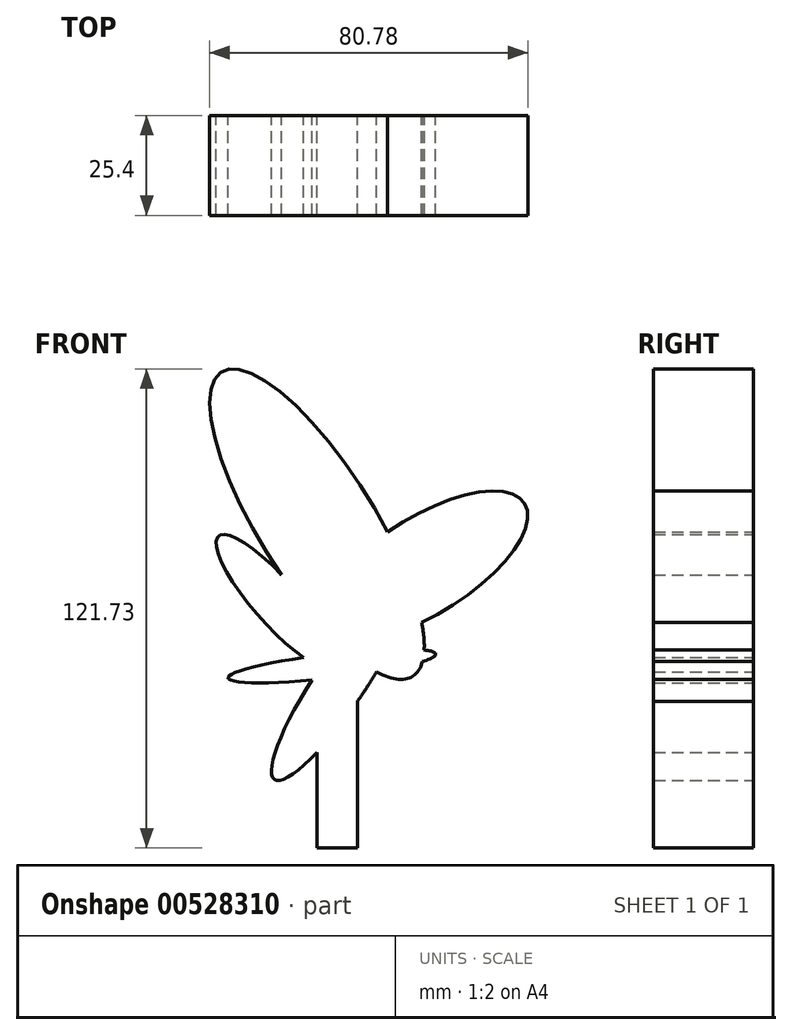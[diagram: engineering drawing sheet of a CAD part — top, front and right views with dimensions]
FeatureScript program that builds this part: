
annotation { "Feature Type Name" : "Feature", "Feature Type Description" : "" }
export const myFeature = defineFeature(function(context is Context, id is Id, definition is map)
    precondition{}
    {
        {
            var Q0;
            Q0=qCreatedBy(makeId("Front.planeOp"),FACE);
            var sketch = newSketch(context, id + "F0", { "sketchPlane" : qUnion([Q0])});
            skLineSegment(sketch, "E0", {"start": v(-21.42, 2.55) * mm, "end": v(-21.42, -21.8) * mm});
            skLineSegment(sketch, "E1", {"start": v(-11.19, 15.4) * mm, "end": v(-11.19, -21.8) * mm});
            skEllipticalArc(sketch, "E2", {});
            skEllipticalArc(sketch, "E3", {});
            skEllipticalArc(sketch, "E4", {});
            skEllipticalArc(sketch, "E5.trimOffspring", {});
            skEllipticalArc(sketch, "E6.trimOffspring", {});
            skEllipticalArc(sketch, "E7.trimOffspring", {});
            skEllipticalArc(sketch, "E8.trimOffspring", {});
            skEllipticalArc(sketch, "E9.trimOffspring", {});
            skEllipticalArc(sketch, "E10.trimOffspring", {});
            skPoint(sketch, "E11.orphan", {"position": v(-21.42, 19.53) * mm});
            skLineSegment(sketch, "E12", {"start": v(-21.42, -21.8) * mm, "end": v(-11.19, -21.8) * mm});
            skEllipticalArc(sketch, "E13.trimOffspring", {});
            const initialGuessF0  = {"E2": [-0.03204191848635339, 0.040952984243628865, 0.6578915012340197, -0.75311272237564, 0.021902368200880307, 0.0056739378525159905, 1.754059745511126, 5.502237001774265], "E3": [0.006067109759896994, 0.05005364865064621, -0.8483565072771697, -0.5294253833737872, 0.029723851108698438, 0.012318866726651034, 1.283638110579809, 4.833864496009394], "E4": [-0.021424479782577985, 0.06048149242996919, 0.5314910901465612, -0.8470638825347354, 0.045661041475952874, 0.014620046839002173, 5.771778276653766, 0.28550303601651894], "E5.trimOffspring": [-0.01763253659009599, 0.024458032101390248, 0.9934402020267449, 0.11435280930987413, 0.02652802497607398, 0.0030641987160904614, 1.8335367287470163, 4.506809050935362], "E6.trimOffspring": [-0.015736564993858337, 0.019907701760530472, 0.5621332872852445, 0.8270466536573888, 0.02934349237690796, 0.00630383582116573, 1.6769998929027905, 4.0712272845825535], "E7.trimOffspring": [-0.01763253659009599, 0.024458032101390248, 0.9934402020267449, 0.11435280930987413, 0.02652802497607398, 0.0030641987160904614, 5.142204103122987, 5.142842324959398], "E8.trimOffspring": [-0.01763253659009599, 0.024458032101390248, 0.9934402020267449, 0.11435280930987413, 0.02652802497607398, 0.0030641987160904614, 5.7583089610562626, 0.4625608624156594], "E9.trimOffspring": [-0.021424479782577985, 0.06048149242996919, 0.5314910901465612, -0.8470638825347354, 0.045661041475952874, 0.014620046839002173, 0.4285865127427125, 0.6892227449294921], "E10.trimOffspring": [-0.021424479782577985, 0.06048149242996919, 0.5314910901465612, -0.8470638825347354, 0.045661041475952874, 0.014620046839002173, 1.3228067359482067, 4.8459614790566565], "E13.trimOffspring": [-0.015736564993858337, 0.019907701760530472, 0.5621332872852445, 0.8270466536573888, 0.02934349237690796, 0.00630383582116573, 4.672422493033295, 4.9820534354491715]};
            skSetInitialGuess(sketch, initialGuessF0);
            skSolve(sketch);
        }
        {
            var Q0;
            Q0=makeQuery(id+"F0.imprint","IMPRINT",FACE,{"disambiguationData":[TD([[makeQuery(id+"F0.imprint","IMPRINT",EDGE,{"derivedFrom":sQuery(id+"F0.wireOp",EDGE,"E0")}),1.0]])]});
            extrude(context, id + "F1", {"entities" : qUnion([Q0]), "depth" : 25.4 * mm, "offsetDistance" : 25.4 * mm});
        }
    });
